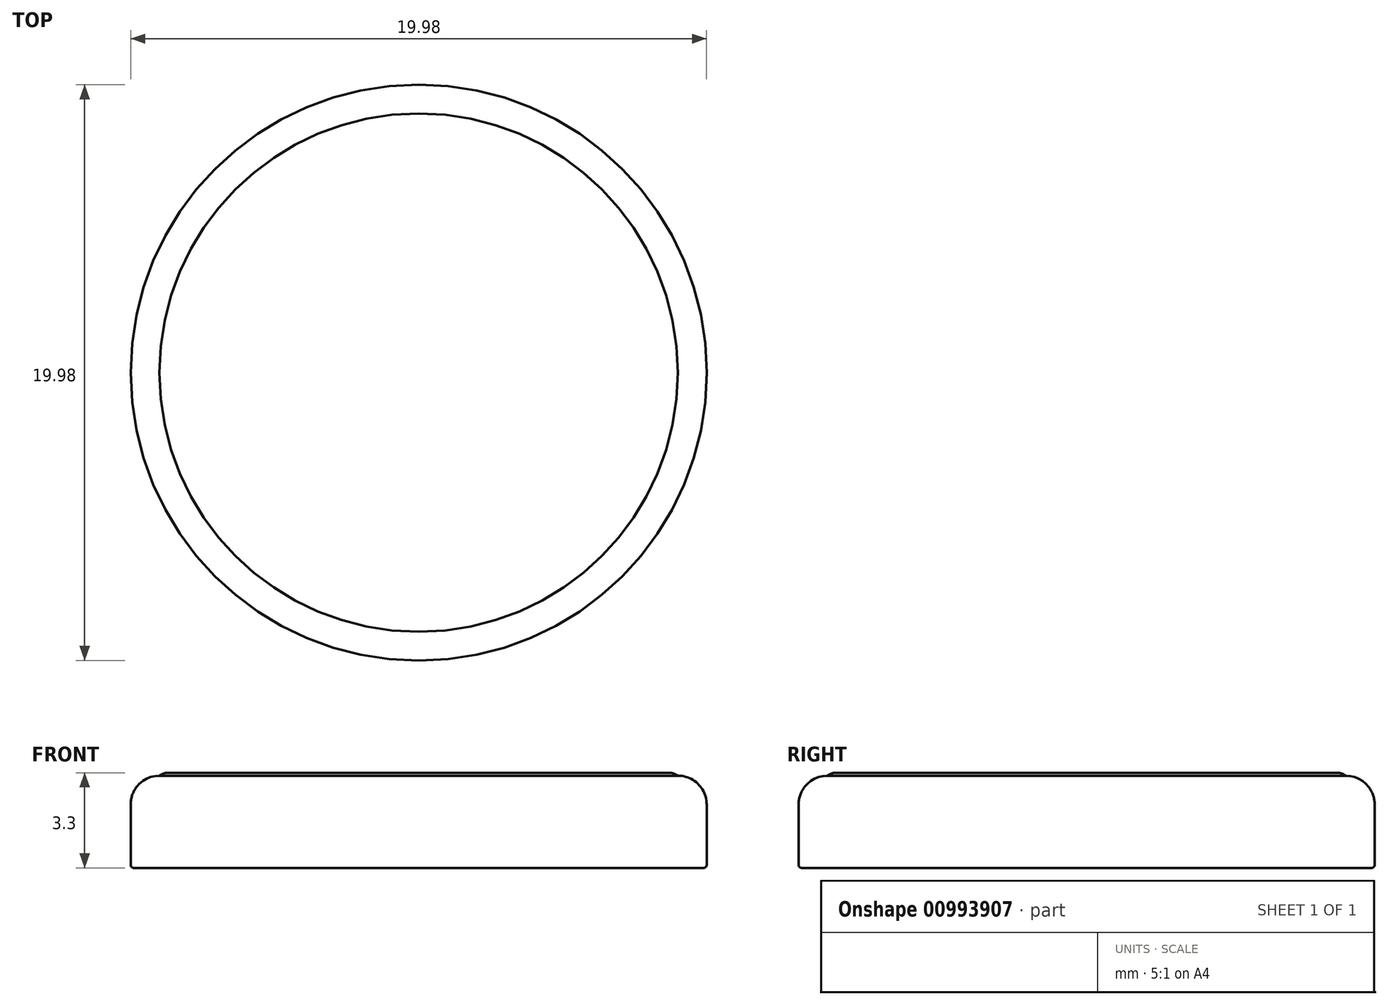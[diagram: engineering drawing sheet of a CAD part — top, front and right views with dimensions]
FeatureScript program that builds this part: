
annotation { "Feature Type Name" : "Feature", "Feature Type Description" : "" }
export const myFeature = defineFeature(function(context is Context, id is Id, definition is map)
    precondition{}
    {
        {
            var Q0;
            Q0=qCreatedBy(makeId("Top.planeOp"),FACE);
            var sketch = newSketch(context, id + "F0", { "sketchPlane" : qUnion([Q0])});
            skCircle(sketch, "E0", {"center": v(0, 0) * mm, "radius": 10 * mm});
            skSolve(sketch);
        }
        {
            var Q0;
            Q0 = qSketchRegion(id + "F0", true);
            extrude(context, id + "F1", {"entities" : qUnion([Q0]), "depth" : 3.2 * mm, "offsetDistance" : 25.4 * mm});
        }
        {
            var Q0;
            Q0=makeQuery(id+"F1.opExtrude","CAP_EDGE",EDGE,{"disambiguationData":[OSD([sQuery(id+"F0.wireOp",EDGE,"E0")])],"isStart":false});
            fillet(context, id + "F2", {"entities" : qUnion([Q0]), "radius" : 1 * mm, "tangentPropagation" : true, "allowEdgeOverflow" : false});
        }
        {
            var Q0;
            Q0=makeQuery(id+"F1.opExtrude","CAP_EDGE",EDGE,{"disambiguationData":[OSD([sQuery(id+"F0.wireOp",EDGE,"E0")])],"isStart":true});
            fillet(context, id + "F3", {"entities" : qUnion([Q0]), "radius" : .1 * mm, "tangentPropagation" : true, "allowEdgeOverflow" : false});
        }
        {
            var Q0;
            Q0=makeQuery(id+"F1.opExtrude","CAP_FACE",FACE,{"disambiguationData":[OSD([sQuery(id+"F0.wireOp",EDGE,"E0")])],"isStart":false});
            var sketch = newSketch(context, id + "F4", { "sketchPlane" : qUnion([Q0])});
            skCircle(sketch, "E1.0.0", {"center": v(0, 0) * mm, "radius": 9 * mm});
            skSolve(sketch);
        }
        {
            var Q0;
            Q0 = qSketchRegion(id + "F4", true);
            extrude(context, id + "F5", {"entities" : qUnion([Q0]), "operationType" : NewBodyOperationType.ADD, "depth" : .1 * mm, "offsetDistance" : 25.4 * mm});
        }
        {
            var Q0;
            Q0=makeQuery(id+"F5.opExtrude","CAP_EDGE",EDGE,{"disambiguationData":[OSD([sQuery(id+"F4.wireOp",EDGE,"E1.0.0")])],"isStart":false});
            fillet(context, id + "F6", {"entities" : qUnion([Q0]), "radius" : .5 * mm, "tangentPropagation" : true, "allowEdgeOverflow" : false});
        }
    });
